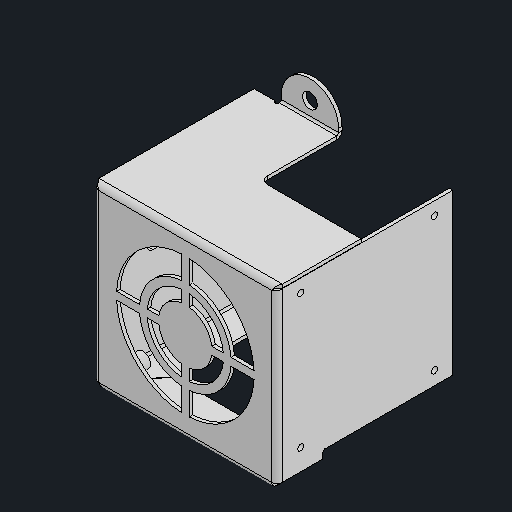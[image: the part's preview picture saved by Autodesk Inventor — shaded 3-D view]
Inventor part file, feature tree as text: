
AUTODESK INVENTOR PART (.ipt)
format: ipt  version: 2024.2 (Build 282272000, 272)  size: 220,160 bytes
history: native  units: mm
features: other x1, sketch x1
ambient origin geometry x8: Origin, YZ Plane, XZ Plane, XY Plane, X Axis, Y Axis, Z Axis, Center Point
bodies: Body1 (feature_tree)
feature tree (2):
  other  "솔리드1"
  sketch  "Sketched Bend2"
